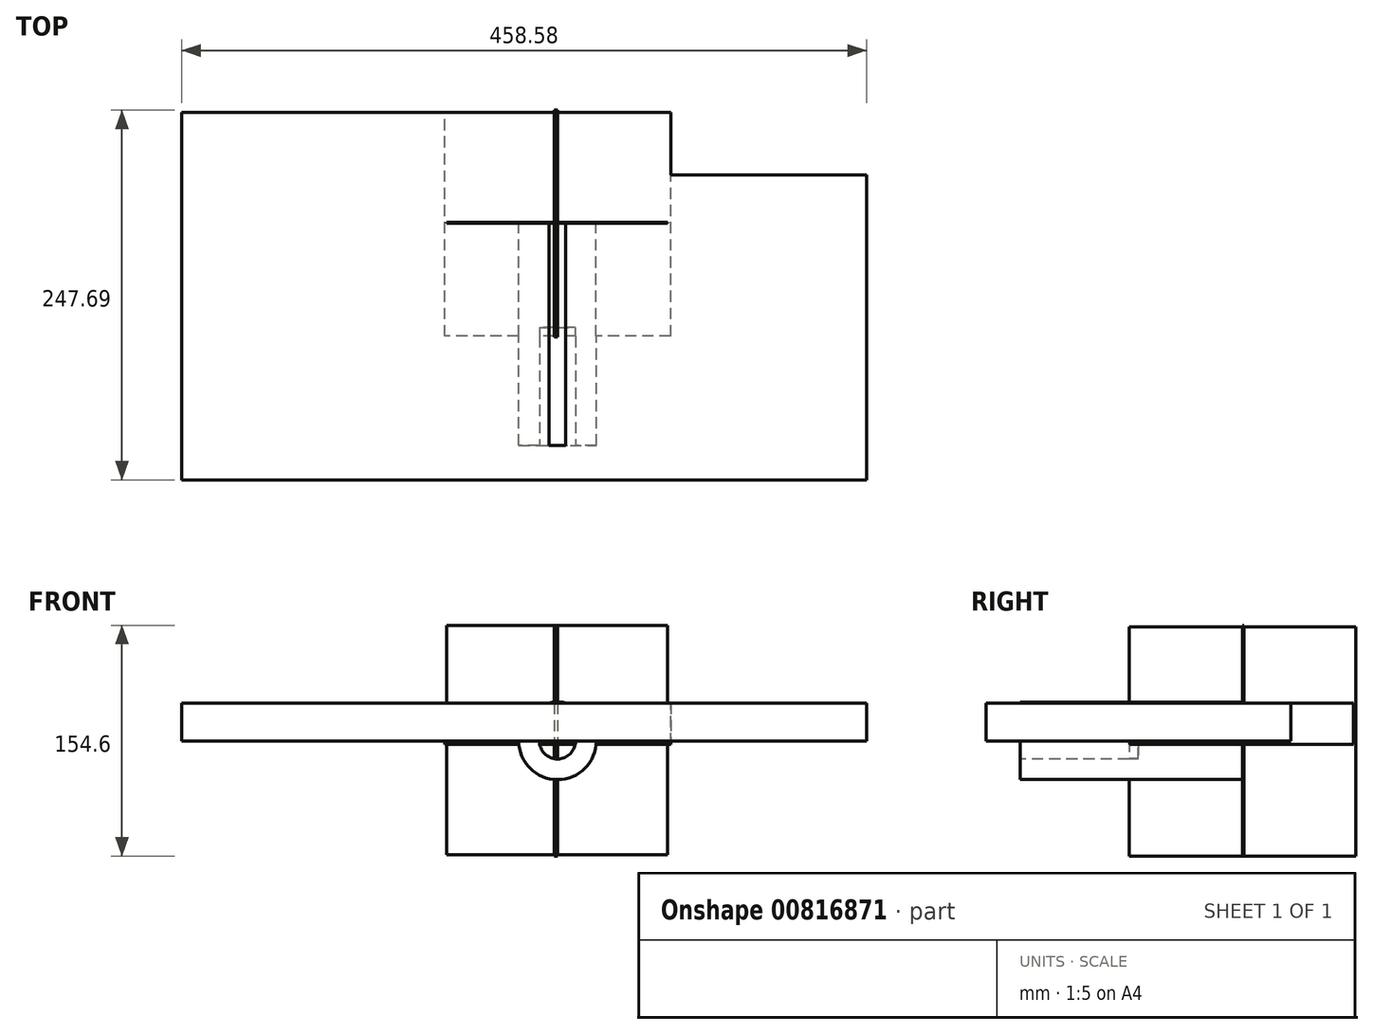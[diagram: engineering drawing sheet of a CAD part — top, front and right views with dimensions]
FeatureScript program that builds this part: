
annotation { "Feature Type Name" : "Feature", "Feature Type Description" : "" }
export const myFeature = defineFeature(function(context is Context, id is Id, definition is map)
    precondition{}
    {
        {
            var Q0;
            Q0=qCreatedBy(makeId("Front.planeOp"),FACE);
            var sketch = newSketch(context, id + "F0", { "sketchPlane" : qUnion([Q0])});
            skCircle(sketch, "E0", {"center": v(0, 0) * mm, "radius": 25.99 * mm});
            skSolve(sketch);
        }
        {
            var Q0;
            Q0=makeQuery(id+"F0.imprint","IMPRINT",FACE,{"disambiguationData":[TD([[makeQuery(id+"F0.imprint","IMPRINT",EDGE,{"derivedFrom":sQuery(id+"F0.wireOp",EDGE,"E0")}),1.0]])]});
            extrude(context, id + "F1", {"entities" : qUnion([Q0]), "depth" : 148.8 * mm, "offsetDistance" : 25.4 * mm});
        }
        {
            var Q0;
            Q0=makeQuery(id+"F1.opExtrude","CAP_FACE",FACE,{"disambiguationData":[OSD([sQuery(id+"F0.wireOp",EDGE,"E0")])],"isStart":false});
            var sketch = newSketch(context, id + "F2", { "sketchPlane" : qUnion([Q0])});
            skCircle(sketch, "E1", {"center": v(0, 0) * mm, "radius": 12.12 * mm});
            skSolve(sketch);
        }
        {
            var Q0;
            Q0 = qSketchRegion(id + "F2", true);
            extrude(context, id + "F3", {"entities" : qUnion([Q0]), "operationType" : NewBodyOperationType.REMOVE, "oppositeDirection" : true, "depth" : 78.89 * mm, "offsetDistance" : 25.4 * mm});
        }
        {
            var Q0;
            Q0=makeQuery(id+"F3.boolean.opBoolean","COPY",FACE,{"derivedFrom":makeQuery(id+"F3.opExtrude","CAP_FACE",FACE,{"disambiguationData":[OSD([sQuery(id+"F2.wireOp",EDGE,"E1")])],"isStart":false})});
            var sketch = newSketch(context, id + "F4", { "sketchPlane" : qUnion([Q0])});
            skCircle(sketch, "E2", {"center": v(-6, 0) * mm, "radius": 12.5 * mm});
            skSolve(sketch);
        }
        {
            var Q0;
            Q0 = qSketchRegion(id + "F4", true);
            extrude(context, id + "F5", {"entities" : qUnion([Q0]), "operationType" : NewBodyOperationType.ADD, "oppositeDirection" : true, "depth" : 42.68 * mm, "offsetDistance" : 25.4 * mm});
        }
        {
            var Q0;
            Q0=qCreatedBy(makeId("Top.planeOp"),FACE);
            var sketch = newSketch(context, id + "F6", { "sketchPlane" : qUnion([Q0])});
            skLineSegment(sketch, "E3.bottom", {"start": v(75.84, -75.6) * mm, "end": v(-75.43, -75.6) * mm});
            skLineSegment(sketch, "E3.top", {"start": v(75.84, 74.32) * mm, "end": v(-75.43, 74.32) * mm});
            skLineSegment(sketch, "E3.left", {"start": v(75.84, -75.6) * mm, "end": v(75.84, 74.32) * mm});
            skLineSegment(sketch, "E3.right", {"start": v(-75.43, -75.6) * mm, "end": v(-75.43, 74.32) * mm});
            skSolve(sketch);
        }
        {
            var Q0;
            Q0 = qSketchRegion(id + "F6", true);
            extrude(context, id + "F7", {"entities" : qUnion([Q0]), "operationType" : NewBodyOperationType.ADD, "oppositeDirection" : true, "depth" : 2.3 * mm, "offsetDistance" : 25.4 * mm});
        }
        {
            var Q0;
            Q0=qCreatedBy(makeId("Right.planeOp"),FACE);
            var sketch = newSketch(context, id + "F8", { "sketchPlane" : qUnion([Q0])});
            skLineSegment(sketch, "E4.bottom", {"start": v(-76, 76.44) * mm, "end": v(75.82, 76.44) * mm});
            skLineSegment(sketch, "E4.top", {"start": v(-76, -77.15) * mm, "end": v(75.82, -77.15) * mm});
            skLineSegment(sketch, "E4.left", {"start": v(-76, 76.44) * mm, "end": v(-76, -77.15) * mm});
            skLineSegment(sketch, "E4.right", {"start": v(75.82, 76.44) * mm, "end": v(75.82, -77.15) * mm});
            skSolve(sketch);
        }
        {
            var Q0;
            Q0 = qSketchRegion(id + "F8", true);
            extrude(context, id + "F9", {"entities" : qUnion([Q0]), "operationType" : NewBodyOperationType.ADD, "oppositeDirection" : true, "depth" : 2.06 * mm, "offsetDistance" : 25.4 * mm});
        }
        {
            var Q0;
            Q0=qCreatedBy(makeId("Front.planeOp"),FACE);
            var sketch = newSketch(context, id + "F10", { "sketchPlane" : qUnion([Q0])});
            skLineSegment(sketch, "E5.bottom", {"start": v(-74.26, 77.45) * mm, "end": v(73.86, 77.45) * mm});
            skLineSegment(sketch, "E5.top", {"start": v(-74.26, -76.46) * mm, "end": v(73.86, -76.46) * mm});
            skLineSegment(sketch, "E5.left", {"start": v(-74.26, 77.45) * mm, "end": v(-74.26, -76.46) * mm});
            skLineSegment(sketch, "E5.right", {"start": v(73.86, 77.45) * mm, "end": v(73.86, -76.46) * mm});
            skSolve(sketch);
        }
        {
            var Q0;
            Q0 = qSketchRegion(id + "F10", true);
            extrude(context, id + "F11", {"entities" : qUnion([Q0]), "operationType" : NewBodyOperationType.ADD, "oppositeDirection" : true, "depth" : 0.83 * mm, "offsetDistance" : 25.4 * mm});
        }
        {
            var Q0;
            {var subQ0=sQuery(id+"F6.wireOp",EDGE,"E3.bottom");var subQ2=sQuery(id+"F6.wireOp",EDGE,"E3.top");var subQ4=sQuery(id+"F0.wireOp",EDGE,"E0");var subQ5=makeQuery(id+"F1.opExtrude","SWEPT_FACE",FACE,{"disambiguationData":[OSD([subQ4])]});var subQ7=sQuery(id+"F6.wireOp",EDGE,"E3.left");var subQ8=makeQuery(id+"F7.opExtrude","SWEPT_FACE",FACE,{"disambiguationData":[OSD([subQ7])]});var subQ9=sQuery(id+"F6.wireOp",EDGE,"E3.right");Q0=makeQuery(id+"F9.boolean.opBoolean","SPLIT",FACE,{"disambiguationData":[TD([subQ8])],"derivedFrom":makeQuery(id+"F7.boolean.opBoolean","SPLIT",FACE,{"disambiguationData":[TD([subQ5])],"derivedFrom":makeQuery(id+"F7.opExtrude","CAP_FACE",FACE,{"disambiguationData":[OSD([subQ0,subQ2,subQ7,subQ9])],"isStart":true})})});}
            var sketch = newSketch(context, id + "F12", { "sketchPlane" : qUnion([Q0])});
            skLineSegment(sketch, "E6.bottom", {"start": v(75.84, 74.32) * mm, "end": v(-251.62, 74.32) * mm});
            skLineSegment(sketch, "E6.top", {"start": v(75.84, 32.36) * mm, "end": v(-251.62, 32.36) * mm});
            skLineSegment(sketch, "E6.left", {"start": v(75.84, 74.32) * mm, "end": v(75.84, 32.36) * mm});
            skLineSegment(sketch, "E6.right", {"start": v(-251.62, 74.32) * mm, "end": v(-251.62, 32.36) * mm});
            skLineSegment(sketch, "E7.bottom", {"start": v(-251.62, 32.36) * mm, "end": v(206.96, 32.36) * mm});
            skLineSegment(sketch, "E7.top", {"start": v(-251.62, -171.87) * mm, "end": v(206.96, -171.87) * mm});
            skLineSegment(sketch, "E7.left", {"start": v(-251.62, 32.36) * mm, "end": v(-251.62, -171.87) * mm});
            skLineSegment(sketch, "E7.right", {"start": v(206.96, 32.36) * mm, "end": v(206.96, -171.87) * mm});
            skSolve(sketch);
        }
        {
            var Q0;
            Q0 = qSketchRegion(id + "F12", true);
            extrude(context, id + "F13", {"entities" : qUnion([Q0]), "operationType" : NewBodyOperationType.ADD, "depth" : 25.4 * mm, "offsetDistance" : 25.4 * mm});
        }
    });
